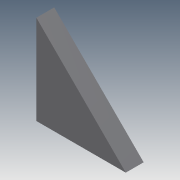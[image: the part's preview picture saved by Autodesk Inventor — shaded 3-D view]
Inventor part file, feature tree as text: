
AUTODESK INVENTOR PART (.ipt)
format: ipt  version: 2011 (Build 150239000, 239)  size: 64,512 bytes
history: native  units: in
note: dims shown in document units (in); Inventor stores cm internally (conversion verified against a paired STEP export)
features: extrude x1, sketch x1
ambient origin geometry x8: Origin, YZ Plane, XZ Plane, XY Plane, X Axis, Y Axis, Z Axis, Center Point
bodies: Solid1 (feature_tree)
feature tree (2):
  extrude  "Extrusion1"  Depth=1.25in
  sketch  "Sketch1"  dims[d0=1.25in d1=1.25in d2=0.25in d3=0.0in]
